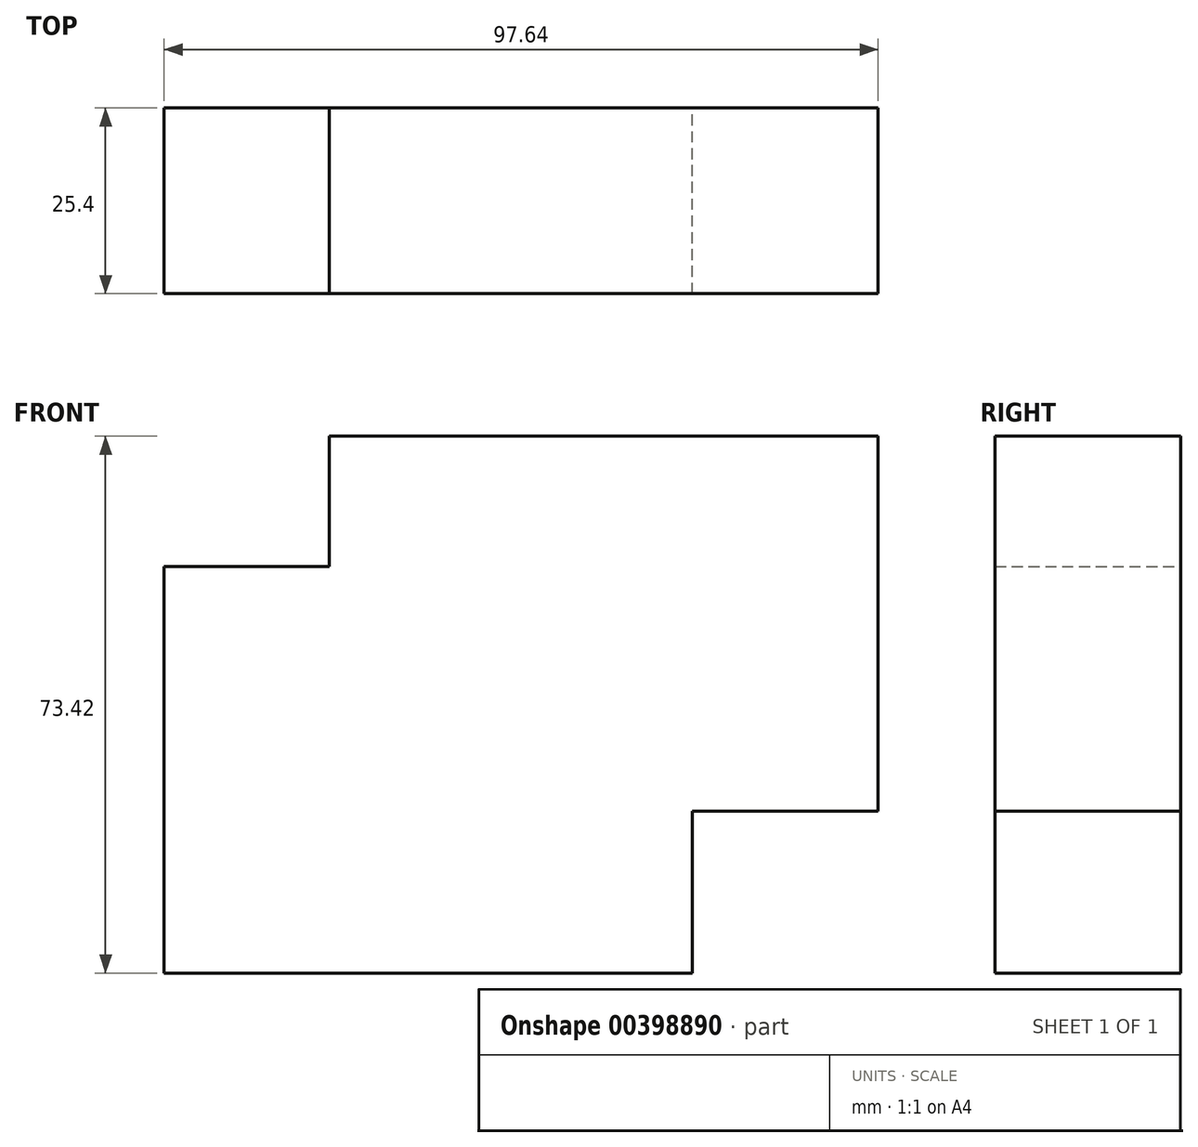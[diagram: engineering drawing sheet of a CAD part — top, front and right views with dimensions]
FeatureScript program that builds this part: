
annotation { "Feature Type Name" : "Feature", "Feature Type Description" : "" }
export const myFeature = defineFeature(function(context is Context, id is Id, definition is map)
    precondition{}
    {
        {
            var Q0;
            Q0=qCreatedBy(makeId("Front.planeOp"),FACE);
            var sketch = newSketch(context, id + "F0", { "sketchPlane" : qUnion([Q0])});
            skLineSegment(sketch, "E0.bottom", {"start": v(-67.68, 43.2) * mm, "end": v(4.58, 43.2) * mm});
            skLineSegment(sketch, "E0.top", {"start": v(-67.68, -12.42) * mm, "end": v(4.58, -12.42) * mm});
            skLineSegment(sketch, "E0.left", {"start": v(-67.68, 43.2) * mm, "end": v(-67.68, -12.42) * mm});
            skLineSegment(sketch, "E0.right", {"start": v(4.58, 43.2) * mm, "end": v(4.58, -12.42) * mm});
            skLineSegment(sketch, "E1.bottom", {"start": v(-45.12, 61) * mm, "end": v(29.96, 61) * mm});
            skLineSegment(sketch, "E1.top", {"start": v(-45.12, 9.7) * mm, "end": v(29.96, 9.7) * mm});
            skLineSegment(sketch, "E1.left", {"start": v(-45.12, 61) * mm, "end": v(-45.12, 9.7) * mm});
            skLineSegment(sketch, "E1.right", {"start": v(29.96, 61) * mm, "end": v(29.96, 9.7) * mm});
            skSolve(sketch);
        }
        {
            var Q0;
            {var subQ6=sQuery(id+"F0.wireOp",EDGE,"E1.bottom");Q0=makeQuery(id+"F0.imprint","IMPRINT",FACE,{"disambiguationData":[TD([[makeQuery(id+"F0.imprint","IMPRINT",EDGE,{"derivedFrom":subQ6}),-1.0]])]});}
            var Q1;
            {var subQ1=sQuery(id+"F0.wireOp",EDGE,"E0.top");Q1=makeQuery(id+"F0.imprint","IMPRINT",FACE,{"disambiguationData":[TD([[makeQuery(id+"F0.imprint","IMPRINT",EDGE,{"derivedFrom":subQ1}),1.0]])]});}
            var Q2;
            {var subQ0=sQuery(id+"F0.wireOp",EDGE,"E0.right");var subQ1=sQuery(id+"F0.wireOp",EDGE,"E0.bottom");var subQ2=makeQuery(id+"F0.imprint","INTERSECT",VERTEX,{"derivedFrom":[subQ1,subQ0]});Q2=makeQuery(id+"F0.imprint","IMPRINT",FACE,{"disambiguationData":[TD([[makeQuery(id+"F0.imprint","IMPRINT",EDGE,{"disambiguationData":[TD([[subQ2,1.0]])],"derivedFrom":subQ1}),-1.0]])]});}
            extrude(context, id + "F1", {"entities" : qUnion([Q0, Q1, Q2]), "depth" : 25.4 * mm});
        }
    });
